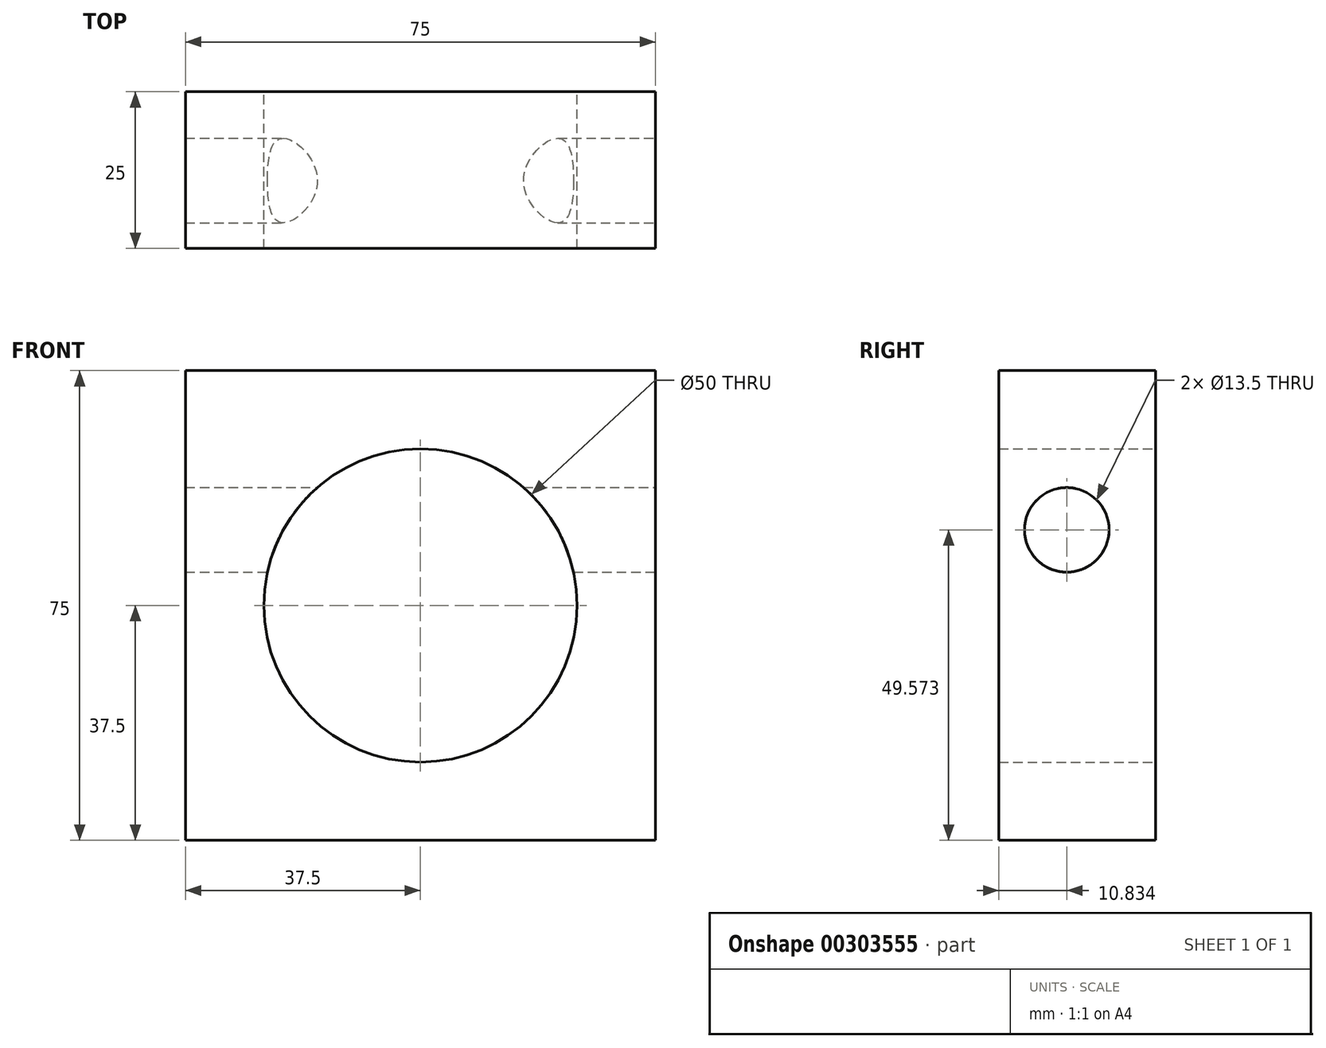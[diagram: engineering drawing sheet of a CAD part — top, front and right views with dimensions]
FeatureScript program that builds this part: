
annotation { "Feature Type Name" : "Feature", "Feature Type Description" : "" }
export const myFeature = defineFeature(function(context is Context, id is Id, definition is map)
    precondition{}
    {
        {
            var Q0;
            Q0=qCreatedBy(makeId("Front.planeOp"),FACE);
            var sketch = newSketch(context, id + "F0", { "sketchPlane" : qUnion([Q0])});
            skLineSegment(sketch, "E0.bottom", {"start": v(0, 0) * mm, "end": v(75, 0) * mm});
            skLineSegment(sketch, "E0.top", {"start": v(0, 75) * mm, "end": v(75, 75) * mm});
            skLineSegment(sketch, "E0.left", {"start": v(0, 0) * mm, "end": v(0, 75) * mm});
            skLineSegment(sketch, "E0.right", {"start": v(75, 0) * mm, "end": v(75, 75) * mm});
            skCircle(sketch, "E1", {"center": v(37.5, 37.5) * mm, "radius": 25 * mm});
            skPoint(sketch, "E1.centerSnap0", {"position": v(37.5, 75) * mm});
            skPoint(sketch, "E1.centerSnap1", {"position": v(0, 37.5) * mm});
            skCircle(sketch, "E2.cCircle", {"center": v(37.5, 37.5) * mm, "radius": 14.58 * mm, "construction": true});
            skLineSegment(sketch, "E2.0", {"start": v(22.33, 44.8) * mm, "end": v(36.23, 54.29) * mm});
            skLineSegment(sketch, "E2.1", {"start": v(36.23, 54.29) * mm, "end": v(51.4, 47) * mm});
            skLineSegment(sketch, "E2.2", {"start": v(51.4, 47) * mm, "end": v(52.67, 30.2) * mm});
            skLineSegment(sketch, "E2.3", {"start": v(52.67, 30.2) * mm, "end": v(38.77, 20.71) * mm});
            skLineSegment(sketch, "E2.4", {"start": v(38.77, 20.71) * mm, "end": v(23.6, 28) * mm});
            skLineSegment(sketch, "E2.5", {"start": v(23.6, 28) * mm, "end": v(22.33, 44.8) * mm});
            skPoint(sketch, "E2.0.midPoint", {"position": v(29.28, 49.54) * mm});
            skLineSegment(sketch, "E3", {"start": v(-18.85, 37.5) * mm, "end": v(91.2, 37.5) * mm, "construction": true});
            skPoint(sketch, "E3.endSnap0", {"position": v(75, 37.5) * mm});
            skCircle(sketch, "E4.1.0", {"center": v(-51.23, 13.73) * mm, "radius": 14.58 * mm, "construction": true});
            skCircle(sketch, "E4.2.0", {"center": v(13.73, -51.23) * mm, "radius": 14.58 * mm, "construction": true});
            skPoint(sketch, "E4.center", {"position": v(0, 0) * mm});
            skSolve(sketch);
        }
        {
            var Q0;
            Q0=makeQuery(id+"F0.imprint","IMPRINT",FACE,{"disambiguationData":[TD([[makeQuery(id+"F0.imprint","IMPRINT",EDGE,{"derivedFrom":sQuery(id+"F0.wireOp",EDGE,"E0.bottom")}),1.0]])]});
            extrude(context, id + "F1", {"entities" : qUnion([Q0]), "depth" : 25 * mm});
        }
        {
            var Q0;
            Q0=makeQuery(id+"F1.opExtrude","SWEPT_FACE",FACE,{"disambiguationData":[OSD([sQuery(id+"F0.wireOp",EDGE,"E0.right")])]});
            var sketch = newSketch(context, id + "F2", { "sketchPlane" : qUnion([Q0])});
            skCircle(sketch, "E5", {"center": v(-14.17, 49.57) * mm, "radius": 6.75 * mm});
            skSolve(sketch);
        }
        {
            var Q0;
            Q0=makeQuery(id+"F2.imprint","IMPRINT",FACE,{"disambiguationData":[TD([[makeQuery(id+"F2.imprint","IMPRINT",EDGE,{"derivedFrom":sQuery(id+"F2.wireOp",EDGE,"E5")}),1.0]])]});
            extrude(context, id + "F3", {"entities" : qUnion([Q0]), "operationType" : NewBodyOperationType.REMOVE, "oppositeDirection" : true, "depth" : 92 * mm});
        }
    });
